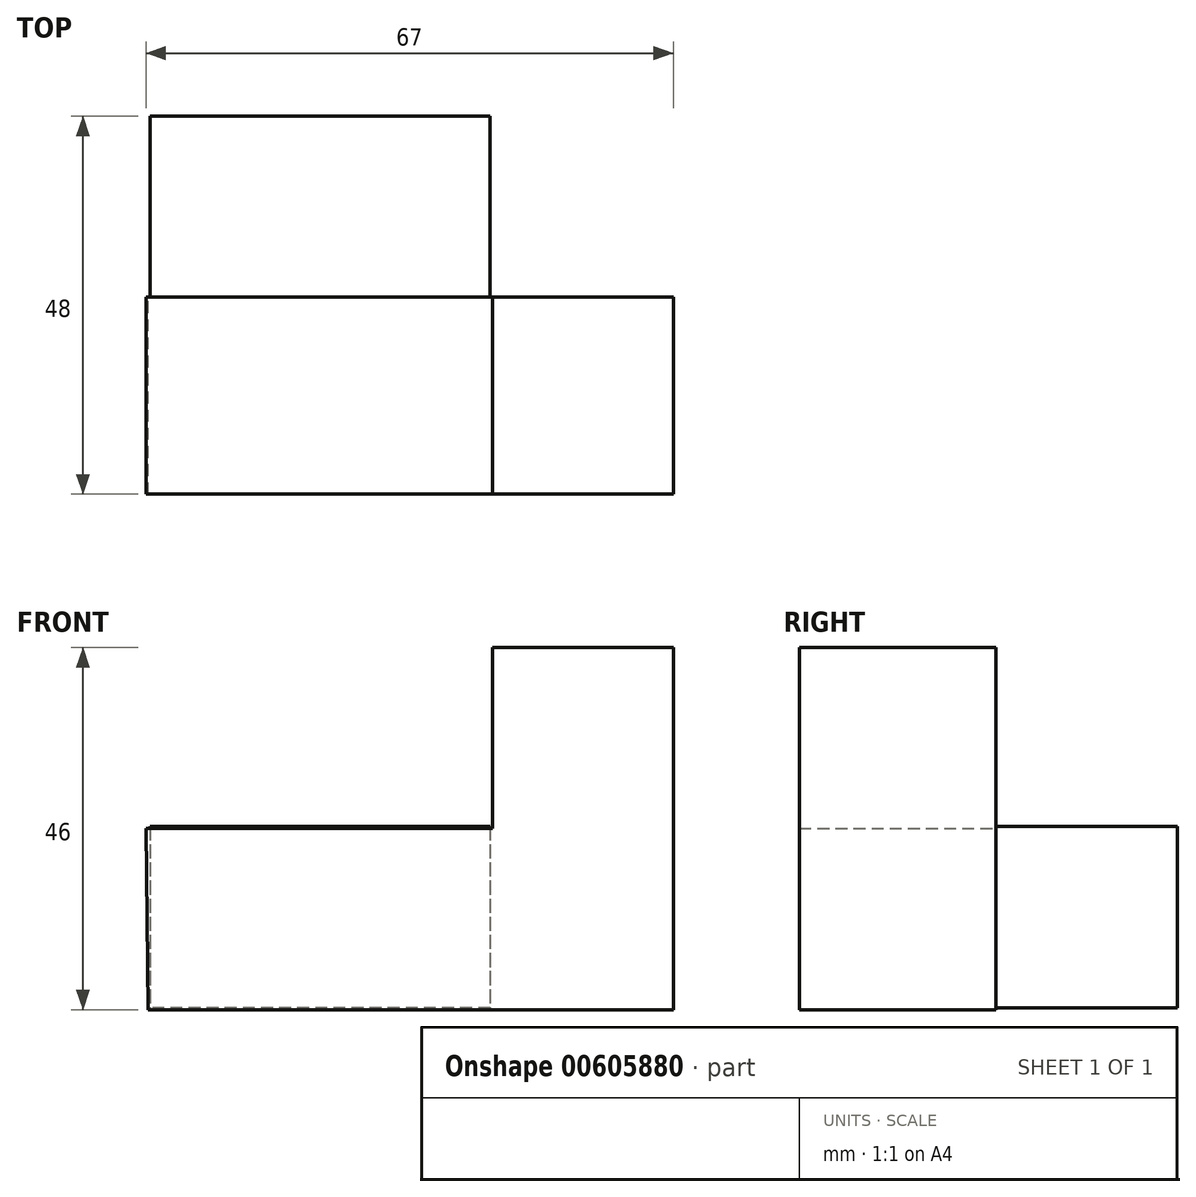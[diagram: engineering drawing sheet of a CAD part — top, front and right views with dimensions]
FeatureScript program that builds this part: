
annotation { "Feature Type Name" : "Feature", "Feature Type Description" : "" }
export const myFeature = defineFeature(function(context is Context, id is Id, definition is map)
    precondition{}
    {
        {
            var Q0;
            Q0=qCreatedBy(makeId("Front.planeOp"),FACE);
            var sketch = newSketch(context, id + "F0", { "sketchPlane" : qUnion([Q0])});
            skLineSegment(sketch, "E0", {"start": v(-29.17, 10.2) * mm, "end": v(14.83, 10.2) * mm});
            skLineSegment(sketch, "E1", {"start": v(14.83, 10.2) * mm, "end": v(14.83, -12.8) * mm});
            skLineSegment(sketch, "E2", {"start": v(14.83, -12.8) * mm, "end": v(-28.87, -12.8) * mm});
            skLineSegment(sketch, "E3", {"start": v(-29.17, 10.2) * mm, "end": v(-28.87, -12.8) * mm});
            skLineSegment(sketch, "E4", {"start": v(14.83, 10.2) * mm, "end": v(37.83, 10.2) * mm});
            skLineSegment(sketch, "E5", {"start": v(37.83, 10.2) * mm, "end": v(37.83, -12.8) * mm});
            skLineSegment(sketch, "E6", {"start": v(14.83, -12.8) * mm, "end": v(37.83, -12.8) * mm});
            skLineSegment(sketch, "E7", {"start": v(14.83, 10.2) * mm, "end": v(14.83, 33.2) * mm});
            skLineSegment(sketch, "E8", {"start": v(14.83, 33.2) * mm, "end": v(37.83, 33.2) * mm});
            skLineSegment(sketch, "E9", {"start": v(37.83, 33.2) * mm, "end": v(37.83, 10.2) * mm});
            skSolve(sketch);
        }
        {
            var Q0;
            Q0 = qSketchRegion(id + "F0", true);
            extrude(context, id + "F1", {"entities" : qUnion([Q0]), "depth" : 25 * mm, "offsetDistance" : 25 * mm});
        }
        {
            var Q0;
            Q0=qCreatedBy(makeId("Front.planeOp"),FACE);
            var sketch = newSketch(context, id + "F2", { "sketchPlane" : qUnion([Q0])});
            skLineSegment(sketch, "E10", {"start": v(14.55, 10.5) * mm, "end": v(14.55, -12.6) * mm});
            skLineSegment(sketch, "E11", {"start": v(14.55, 10.5) * mm, "end": v(-28.65, 10.5) * mm});
            skLineSegment(sketch, "E12", {"start": v(-28.65, 10.5) * mm, "end": v(-28.65, -12.6) * mm});
            skLineSegment(sketch, "E13", {"start": v(14.55, -12.6) * mm, "end": v(-28.65, -12.6) * mm});
            skSolve(sketch);
        }
        {
            var Q0;
            Q0 = qSketchRegion(id + "F2", true);
            extrude(context, id + "F3", {"entities" : qUnion([Q0]), "operationType" : NewBodyOperationType.ADD, "oppositeDirection" : true, "depth" : 23 * mm, "offsetDistance" : 25 * mm});
        }
    });
